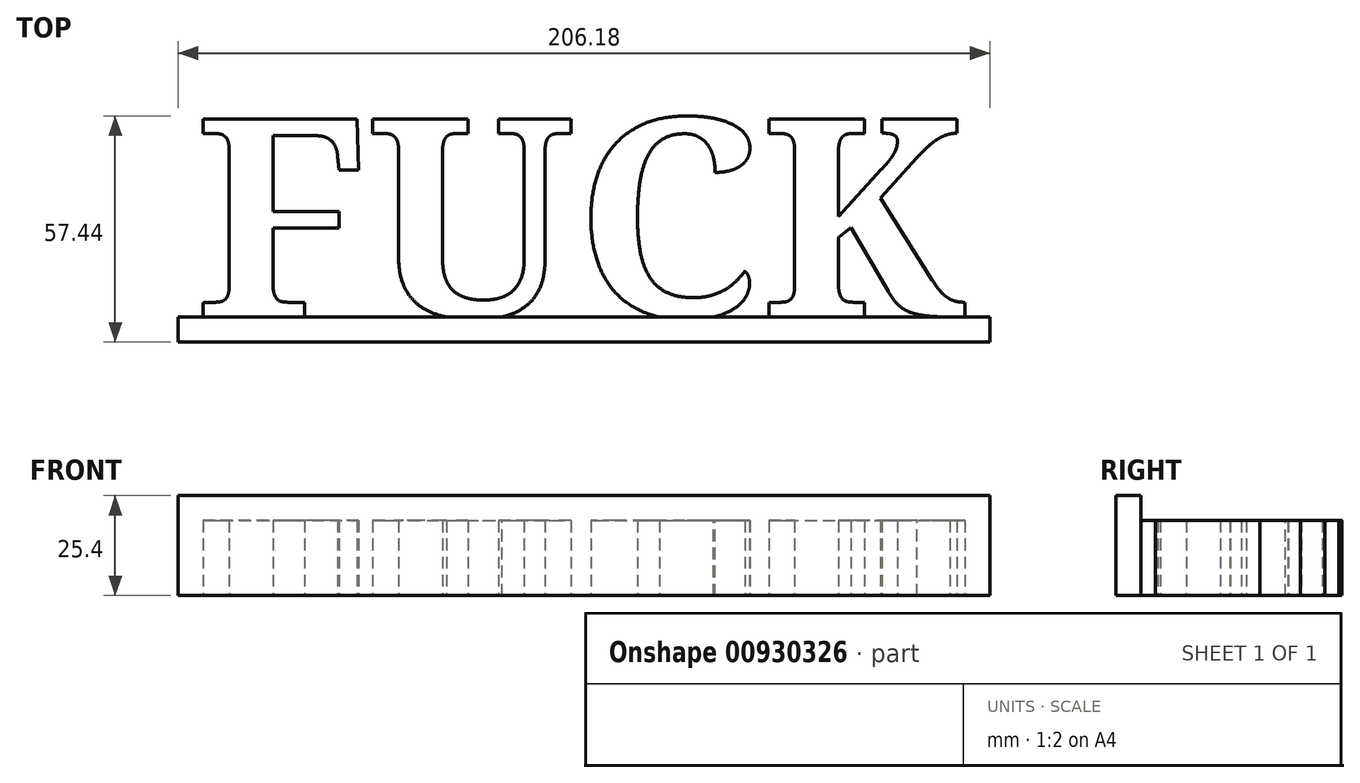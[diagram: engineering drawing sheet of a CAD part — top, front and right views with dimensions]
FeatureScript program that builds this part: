
annotation { "Feature Type Name" : "Feature", "Feature Type Description" : "" }
export const myFeature = defineFeature(function(context is Context, id is Id, definition is map)
    precondition{}
    {
        {
            var Q0;
            Q0=qCreatedBy(makeId("Top.planeOp"),FACE);
            var sketch = newSketch(context, id + "F0", { "sketchPlane" : qUnion([Q0])});
            skText(sketch, "E0", { "text": "FUCK", "fontName": "NotoSerif-Bold.ttf"});
            const initialGuessF0  = {"E0": [0, 0, 1, 0, 0.0508]};
            skSetInitialGuess(sketch, initialGuessF0);
            skSolve(sketch);
        }
        {
            var Q0;
            Q0 = qSketchRegion(id + "F0", true);
            extrude(context, id + "F1", {"entities" : qUnion([Q0]), "depth" : 19.05 * mm, "offsetDistance" : 25.4 * mm});
        }
        {
            var Q0;
            Q0=qCreatedBy(makeId("Top.planeOp"),FACE);
            var sketch = newSketch(context, id + "F2", { "sketchPlane" : qUnion([Q0])});
            skLineSegment(sketch, "E1.bottom", {"start": v(201.79, -6.35) * mm, "end": v(-4.39, -6.35) * mm});
            skLineSegment(sketch, "E1.top", {"start": v(201.79, 0) * mm, "end": v(-4.39, 0) * mm});
            skLineSegment(sketch, "E1.left", {"start": v(201.79, -6.35) * mm, "end": v(201.79, 0) * mm});
            skLineSegment(sketch, "E1.right", {"start": v(-4.39, -6.35) * mm, "end": v(-4.39, 0) * mm});
            skSolve(sketch);
        }
        {
            var Q0;
            Q0 = qSketchRegion(id + "F2", true);
            var Q1;
            Q1=makeQuery(id+"F1.opExtrude","CAP_FACE",FACE,{"disambiguationData":[OSD([sQuery(id+"F0.wireOp",EDGE,"E0.sketch_text.stroke-0"),sQuery(id+"F0.wireOp",EDGE,"E0.sketch_text.stroke-1"),sQuery(id+"F0.wireOp",EDGE,"E0.sketch_text.stroke-2"),sQuery(id+"F0.wireOp",EDGE,"E0.sketch_text.stroke-3"),sQuery(id+"F0.wireOp",EDGE,"E0.sketch_text.stroke-4"),sQuery(id+"F0.wireOp",EDGE,"E0.sketch_text.stroke-5"),sQuery(id+"F0.wireOp",EDGE,"E0.sketch_text.stroke-6"),sQuery(id+"F0.wireOp",EDGE,"E0.sketch_text.stroke-7"),sQuery(id+"F0.wireOp",EDGE,"E0.sketch_text.stroke-8"),sQuery(id+"F0.wireOp",EDGE,"E0.sketch_text.stroke-9"),sQuery(id+"F0.wireOp",EDGE,"E0.sketch_text.stroke-10"),sQuery(id+"F0.wireOp",EDGE,"E0.sketch_text.stroke-11"),sQuery(id+"F0.wireOp",EDGE,"E0.sketch_text.stroke-12"),sQuery(id+"F0.wireOp",EDGE,"E0.sketch_text.stroke-13"),sQuery(id+"F0.wireOp",EDGE,"E0.sketch_text.stroke-14"),sQuery(id+"F0.wireOp",EDGE,"E0.sketch_text.stroke-15"),sQuery(id+"F0.wireOp",EDGE,"E0.sketch_text.stroke-16"),sQuery(id+"F0.wireOp",EDGE,"E0.sketch_text.stroke-17"),sQuery(id+"F0.wireOp",EDGE,"E0.sketch_text.stroke-18"),sQuery(id+"F0.wireOp",EDGE,"E0.sketch_text.stroke-19"),sQuery(id+"F0.wireOp",EDGE,"E0.sketch_text.stroke-20"),sQuery(id+"F0.wireOp",EDGE,"E0.sketch_text.stroke-21"),sQuery(id+"F0.wireOp",EDGE,"E0.sketch_text.stroke-22"),sQuery(id+"F0.wireOp",EDGE,"E0.sketch_text.stroke-23"),sQuery(id+"F0.wireOp",EDGE,"E0.sketch_text.stroke-24"),sQuery(id+"F0.wireOp",EDGE,"E0.sketch_text.stroke-25"),sQuery(id+"F0.wireOp",EDGE,"E0.sketch_text.stroke-26"),sQuery(id+"F0.wireOp",EDGE,"E0.sketch_text.stroke-27"),sQuery(id+"F0.wireOp",EDGE,"E0.sketch_text.stroke-28"),sQuery(id+"F0.wireOp",EDGE,"E0.sketch_text.stroke-29"),sQuery(id+"F0.wireOp",EDGE,"E0.sketch_text.stroke-30"),sQuery(id+"F0.wireOp",EDGE,"E0.sketch_text.stroke-31")])],"isStart":false});
            extrude(context, id + "F3", {"entities" : qUnion([Q0]), "operationType" : NewBodyOperationType.ADD, "endBound" : BoundingType.UP_TO_SURFACE, "depth" : 25.4 * mm, "endBoundEntityFace" : qUnion([Q1]), "hasOffset" : true, "offsetDistance" : 6.35 * mm, "offsetOppositeDirection" : true});
        }
    });
